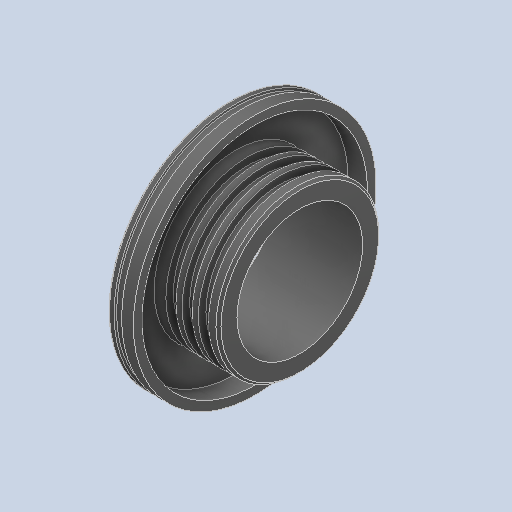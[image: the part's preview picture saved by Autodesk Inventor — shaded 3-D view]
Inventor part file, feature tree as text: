
AUTODESK INVENTOR PART (.ipt)
format: ipt  version: 2024.1 (Build 281209000, 209)  size: 178,688 bytes
history: native  units: in
note: dims shown in document units (in); Inventor stores cm internally (conversion verified against a paired STEP export)
features: fillet x1
ambient origin geometry x8: Origin, YZ Plane, XZ Plane, XY Plane, X Axis, Y Axis, Z Axis, Center Point
bodies: Solid1 (feature_tree)
feature tree (1):
  fillet  "Fillet2"  [1 undecoded]
note: 1 required parameter value undecoded (feature->parameter linkage not recoverable at this tier; creation-order binding heuristic only, values carry confidence <= 0.55)
